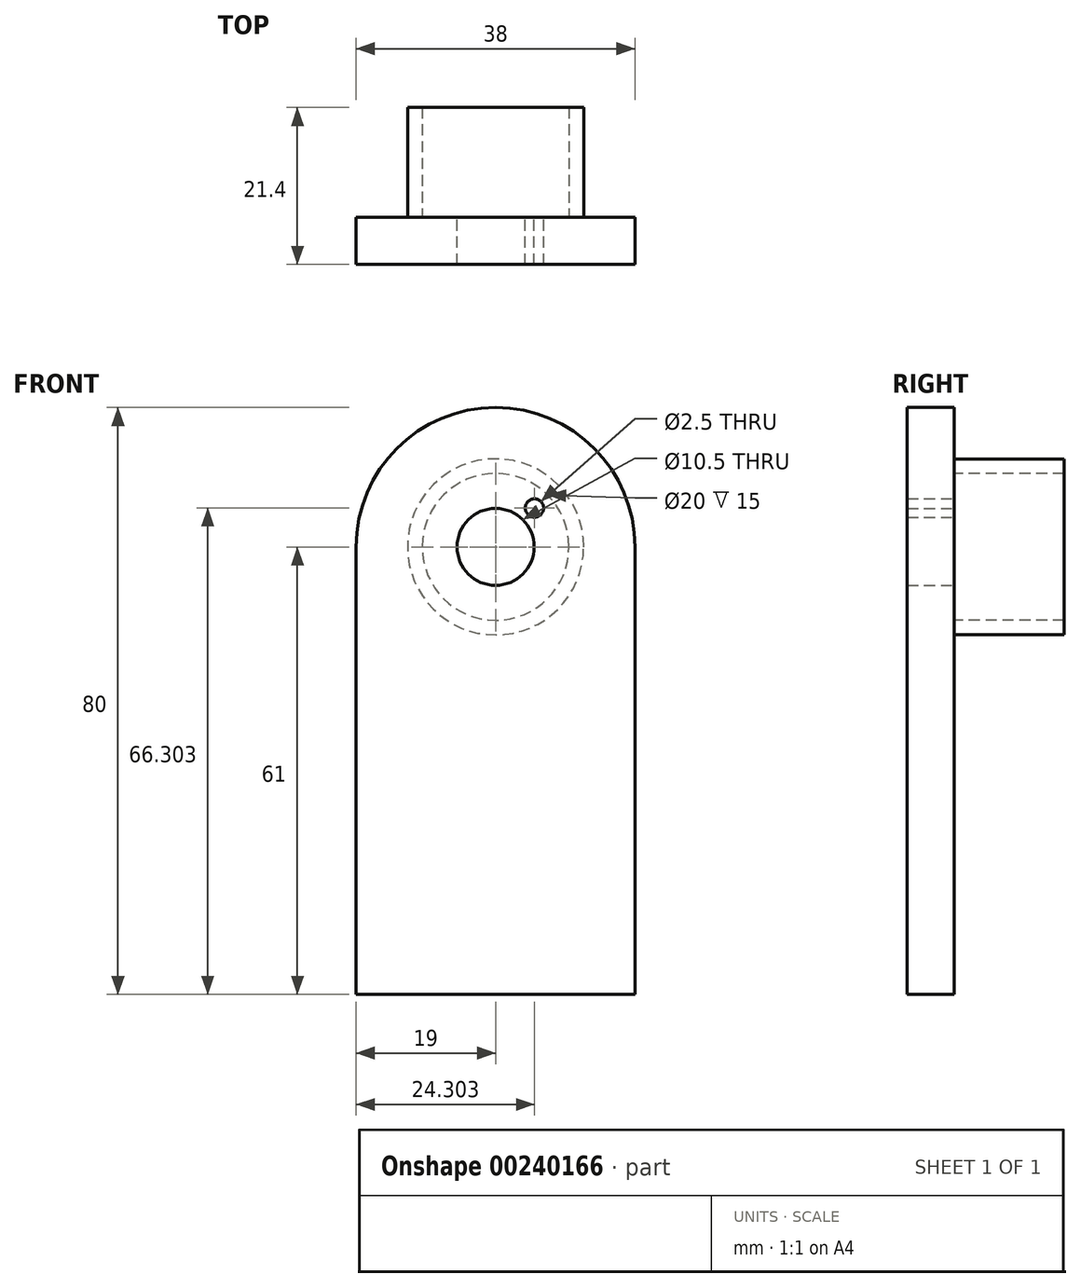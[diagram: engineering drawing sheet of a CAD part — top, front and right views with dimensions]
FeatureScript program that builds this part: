
annotation { "Feature Type Name" : "Feature", "Feature Type Description" : "" }
export const myFeature = defineFeature(function(context is Context, id is Id, definition is map)
    precondition{}
    {
        {
            var Q0;
            Q0=qCreatedBy(makeId("Front.planeOp"),FACE);
            var sketch = newSketch(context, id + "F0", { "sketchPlane" : qUnion([Q0])});
            skLineSegment(sketch, "E0.top", {"start": v(-19, -61) * mm, "end": v(19, -61) * mm});
            skLineSegment(sketch, "E0.left", {"start": v(-19, 0) * mm, "end": v(-19, -61) * mm});
            skLineSegment(sketch, "E0.right", {"start": v(19, 0) * mm, "end": v(19, -61) * mm});
            skArc(sketch, "E1", {"start": v(-19, 0) * mm, "mid": v(0, 19) * mm, "end": v(19, 0) * mm});
            skSolve(sketch);
        }
        {
            var Q0;
            Q0=makeQuery(id+"F0.imprint","IMPRINT",FACE,{"disambiguationData":[TD([[makeQuery(id+"F0.imprint","IMPRINT",EDGE,{"derivedFrom":sQuery(id+"F0.wireOp",EDGE,"E0.top")}),1.0]])]});
            extrude(context, id + "F1", {"entities" : qUnion([Q0]), "depth" : 6.4 * mm});
        }
        {
            var Q0;
            Q0=qCreatedBy(makeId("Front.planeOp"),FACE);
            var sketch = newSketch(context, id + "F2", { "sketchPlane" : qUnion([Q0])});
            skLineSegment(sketch, "E2", {"start": v(0, 0) * mm, "end": v(18.26, 18.26) * mm, "construction": true});
            skCircle(sketch, "E3", {"center": v(0, 0) * mm, "radius": 7.5 * mm, "construction": true});
            skCircle(sketch, "E4", {"center": v(5.3, 5.3) * mm, "radius": 1.25 * mm});
            skSolve(sketch);
        }
        {
            var Q0;
            Q0 = qSketchRegion(id + "F2", true);
            extrude(context, id + "F3", {"entities" : qUnion([Q0]), "operationType" : NewBodyOperationType.REMOVE, "endBound" : BoundingType.THROUGH_ALL, "depth" : 25.4 * mm});
        }
        {
            var Q0;
            Q0=qCreatedBy(makeId("Front.planeOp"),FACE);
            var sketch = newSketch(context, id + "F4", { "sketchPlane" : qUnion([Q0])});
            skCircle(sketch, "E5", {"center": v(0, 0) * mm, "radius": 5.25 * mm});
            skSolve(sketch);
        }
        {
            var Q0;
            Q0=qSketchRegion(id+"F4",true);
            extrude(context, id + "F5", {"entities" : qUnion([Q0]), "operationType" : NewBodyOperationType.REMOVE, "endBound" : BoundingType.THROUGH_ALL, "depth" : 25.4 * mm});
        }
        {
            var Q0;
            Q0=makeQuery(id+"F1.opExtrude","CAP_FACE",FACE,{"disambiguationData":[OSD([sQuery(id+"F0.wireOp",EDGE,"E0.top"),sQuery(id+"F0.wireOp",EDGE,"E0.left"),sQuery(id+"F0.wireOp",EDGE,"E0.right"),sQuery(id+"F0.wireOp",EDGE,"E1")])],"isStart":true});
            var sketch = newSketch(context, id + "F6", { "sketchPlane" : qUnion([Q0])});
            skCircle(sketch, "E6", {"center": v(0, 0) * mm, "radius": 10 * mm});
            skCircle(sketch, "E7", {"center": v(0, 0) * mm, "radius": 12 * mm});
            skSolve(sketch);
        }
        {
            var Q0;
            Q0 = qSketchRegion(id + "F6", true);
            extrude(context, id + "F7", {"entities" : qUnion([Q0]), "operationType" : NewBodyOperationType.ADD, "depth" : 15 * mm});
        }
        {
            var Q0;
            Q0=makeQuery(id+"F1.opExtrude","CAP_EDGE",EDGE,{"disambiguationData":[OSD([sQuery(id+"F0.wireOp",EDGE,"E0.top")])],"isStart":true});
            cPlane(context, id + "F8", {"entities" : qUnion([Q0]), "cplaneType" : CPlaneType.LINE_ANGLE, "offset" : 25 * mm, "angle" : 345 * degree, "width" : 150 * mm, "height" : 150 * mm});
        }
    });
